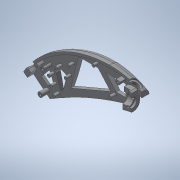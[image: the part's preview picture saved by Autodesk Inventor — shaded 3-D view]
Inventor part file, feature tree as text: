
AUTODESK INVENTOR PART (.ipt)
format: ipt  version: 2020 (Build 240168000, 168)  size: 5,426,176 bytes
history: native  units: in
note: dims shown in document units (in); Inventor stores cm internally (conversion verified against a paired STEP export)
features: extrude x16, sketch x8, other x5, fillet x4, surface_op x2, revolve x2, boolean_combine x1, split x1, chamfer x1, plane x1, delete_face x1, imported_body x1, projected_geometry x1
ambient origin geometry x8: Origin, YZ Plane, XZ Plane, XY Plane, X Axis, Y Axis, Z Axis, Center Point
bodies: Solid1 (feature_tree), Solid196 (feature_tree), Solid197 (feature_tree)
feature tree (44):
  other  "Repaired Geometry1"
  surface_op  "Stitch Surface1"
  sketch  "Sketch2-<F>"  dims[d0=0.03in d1=0.198in]
  extrude  "Extrusion1"  Depth=0.198in
  extrude  "Extrusion2"  Depth=0.184in
  surface_op  "Stitch Surface2"
  boolean_combine  "Combine2"
  split  "Split1"
  extrude  "Extrusion4"  Depth=0.268in
  sketch  "Sketch5-<F>"  dims[d2=0.21in d3=0.184in]
  extrude  "Extrusion5"  Depth=0.4in
  extrude  "Extrusion6"  Depth=0.158in TaperAngle=0.0deg
  extrude  "Extrusion7"  Depth=0.03in
  sketch  "Sketch7-<F>"  dims[d4=0.158in d5=0.0in d7=0.268in]
  extrude  "Extrusion8"  Depth=0.329in
  revolve  "Revolution1"  [1 undecoded]
  revolve  "Revolution2"  [1 undecoded]
  fillet  "Fillet1"  Radius=0.975in
  extrude  "Extrusion9"  Depth=1.086in
  sketch  "Sketch8-<F>"  dims[d8=1.512in d9=0.4in]
  extrude  "Extrusion10"  Depth=0.423in
  extrude  "Extrusion11"  Depth=0.88in
  extrude  "Extrusion12"  Depth=1.0in
  extrude  "Extrusion13"  Depth=1.03in
  chamfer  "Chamfer1"  Distance=1.053in
  extrude  "Extrusion14"  Depth=1.125in
  plane  "Work Plane2"
  extrude  "Extrusion15"  Depth=0.044in
  extrude  "Extrusion16"  Depth=0.09in
  delete_face  "Delete Face2"
  extrude  "Extrusion17"  Depth=0.17in
  fillet  "Fillet3"  Radius=0.24in
  fillet  "Fillet4"  Radius=0.244in
  fillet  "Fillet5"  Radius=0.025in
  other  "Srf3"
  other  "Srf4"
  imported_body  "Base1"
  sketch  "Sketch6-<F>"  dims[d10=0.7in d11=0.158in d12=0.0in]
  sketch  "Sketch9-<F>"  dims[d16=0.004in d17=0.004in d18=0.03in]
  sketch  "Sketch10-<F>"  dims[d19=0.07in]
  projected_geometry  "Projected Loop1"
  sketch  "Sketch11-<F>"  dims[d20=0.031in d45=0.121in d46=0.03in d47=0.158in d48=0.03in d49=0.03in d50=0.03in d51=0.03in d52=0.03in d53=0.03in d54=0.03in d55=0.06in d56=0.03in d57=0.03in d59=0.0962in d60=0.329in d61=0.595in d62=0.85in d63=0.975in d64=1.086in d66=0.423in d67=0.88in d68=1.0in d69=1.03in d70=1.053in d71=1.125in d72=0.044in d73=0.09in d74=0.17in d75=0.24in d76=0.244in d77=0.025in d78=0.016in d79=0.097in d80=0.23in d83=0.225in d84=0.4in d85=0.4055in d86=0.4785in d87=0.4in d88=0.05in d89=1.2in d90=0.0625in d91=0.0in d92=0.2205in d93=0.0206in d94=0.0495in d95=0.0in d96=0.0755in d97=0.0in d124=0.043in d131=0.055in d132=0.11in d133=0.055in d134=0.0235in d135=0.086in d136=0.043in d139=0.045in d141=0.043in d147=0.0235in d148=0.11in d149=0.055in d150=0.2508in d151=0.075in d153=0.0035in d154=0.0035in d155=0.043in d156=0.045in d157=0.055in d158=0.0in d159=90.0deg d160=90.0deg d161=0.04in d162=0.091in d163=0.034in d164=0.064in d165=0.3105in d166=0.025in d167=0.025in d168=0.025in d169=0.025in d170=1.065in d171=1.0in d172=0.0in d173=0.126in d174=0.101in d175=0.108in d176=0.02in d177=0.0in d178=0.009in d179=0.009in d181=1.5748in d183=360.0deg d185=0.012in d186=0.0in d187=0.02in d188=0.0in d189=1.0in d190=0.0in d191=0.02in d192=0.125in d193=0.1374in d194=0.1271in d195=0.159in d196=0.05in d197=0.237in d198=0.317in d199=0.023in d200=1.115in d201=0.2205in d202=0.0in d203=0.07in d204=0.3in d205=-0.1175in d206=0.023in d207=0.0in d208=0.015in d209=0.0in d211=0.03in d212=0.15in d213=0.061in d214=0.0in d216=0.059in d217=0.015in d218=0.004in d219=0.015in d220=0.03in d221=0.059in d222=0.15in d223=0.015in d224=0.275in d225=0.4989in d226=0.014in d227=0.1099in d228=0.015in d229=0.0618in d230=0.014in d231=0.05in]
  other  "OffsetSrf2"
  other  "OffsetSrf1"
note: 2 required parameter values undecoded (feature->parameter linkage not recoverable at this tier; creation-order binding heuristic only, values carry confidence <= 0.55)
